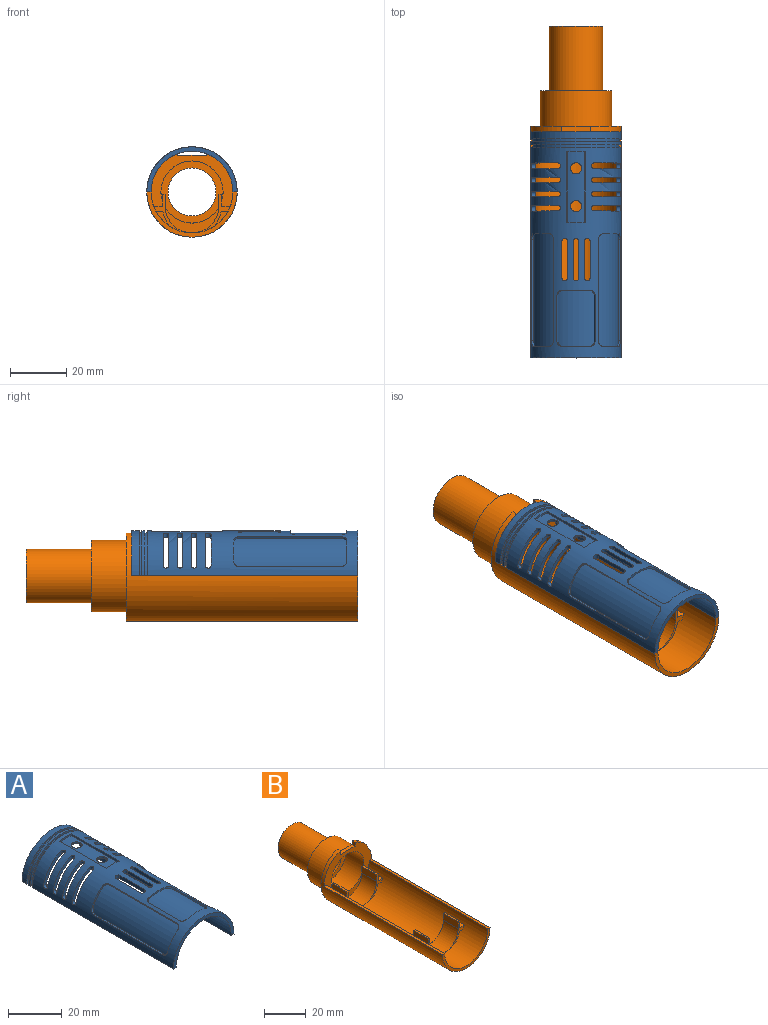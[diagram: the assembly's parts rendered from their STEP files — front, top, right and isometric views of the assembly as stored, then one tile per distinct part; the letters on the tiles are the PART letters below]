
ASSEMBLY  parts=2 mates=1
PART A: 92 faces, bbox 32x80x16 mm
  f0: cylinder r=16mm len=32mm, axis (0,1,0), area 50.3mm2, adj f5,f6,f87,f91
  f1: cylinder r=16mm len=32mm, axis (0,1,0), area 125.7mm2, adj f5,f6,f8,f88
  f2: cylinder r=14.5mm len=80mm, axis (0,1,0), area 3293.1mm2, adj f5,f6,f7,f8,f13,f14,f15,f16
  f3: cylinder r=15.25mm len=25mm, axis (0,1,0), area 134.5mm2, adj f9,f10,f11,f12,f45,f46
  f4: cylinder r=16mm len=74.5mm, axis (0,1,0), area 1885.3mm2, adj f5,f6,f7,f9,f10,f11,f12,f13
  f5: plane 80x1.5mm, normal (0,0,-1), area 118.5mm2, adj f0,f1,f2,f4,f7,f8,f86,f87
  f6: plane 80x1.5mm, normal (0,0,-1), area 118.5mm2, adj f0,f1,f2,f4,f7,f8,f86,f87
  f7: plane 32x16mm, normal (0,-1,0), area 71.9mm2, adj f2,f4,f5,f6
  f8: plane 32x16mm, normal (0,1,0), area 71.9mm2, adj f1,f2,f5,f6
  f9: plane 25x0.73mm, normal (0.98,0,0.21), area 18.8mm2, adj f3,f4,f11,f12
  f10: plane 25x0.73mm, normal (-0.98,0,0.21), area 18.8mm2, adj f3,f4,f11,f12
  f11: plane 6.65x1.08mm, normal (0,1,0), area 4.9mm2, adj f3,f4,f9,f10
  f12: plane 6.65x1.08mm, normal (0,-1,0), area 4.9mm2, adj f3,f4,f9,f10
  f13: plane 11.17x9.67mm, normal (0,-1,0), area 21mm2, adj f2,f4,f17,f18
  f14: plane 11.17x9.67mm, normal (0,1,0), area 21mm2, adj f2,f4,f17,f18
  f15: plane 11.17x9.67mm, normal (0,-1,0), area 21mm2, adj f2,f4,f19,f20
  f16: plane 11.17x9.67mm, normal (0,1,0), area 21mm2, adj f2,f4,f19,f20
  f17: cylinder r=1mm len=2mm, axis (-0.98,0,-0.17), area 4.7mm2, adj f2,f4,f13,f14
  f18: cylinder r=1mm len=2mm, axis (0.34,0,0.94), area 4.7mm2, adj f2,f4,f13,f14
  f19: cylinder r=1mm len=2mm, axis (-0.98,0,0.17), area 4.7mm2, adj f2,f4,f15,f16
  f20: cylinder r=1mm len=2mm, axis (0.34,0,-0.94), area 4.7mm2, adj f2,f4,f15,f16
  f21: plane 11.17x9.67mm, normal (0,-1,0), area 21mm2, adj f2,f4,f25,f26
  f22: plane 11.17x9.67mm, normal (0,1,0), area 21mm2, adj f2,f4,f25,f26
  f23: plane 11.17x9.67mm, normal (0,-1,0), area 21mm2, adj f2,f4,f27,f28
  f24: plane 11.17x9.67mm, normal (0,1,0), area 21mm2, adj f2,f4,f27,f28
  f25: cylinder r=1mm len=2mm, axis (-0.98,0,-0.17), area 4.7mm2, adj f2,f4,f21,f22
  f26: cylinder r=1mm len=2mm, axis (0.34,0,0.94), area 4.7mm2, adj f2,f4,f21,f22
  f27: cylinder r=1mm len=2mm, axis (-0.98,0,0.17), area 4.7mm2, adj f2,f4,f23,f24
  f28: cylinder r=1mm len=2mm, axis (0.34,0,-0.94), area 4.7mm2, adj f2,f4,f23,f24
  f29: plane 11.17x9.67mm, normal (0,-1,0), area 21mm2, adj f2,f4,f33,f34
  f30: plane 11.17x9.67mm, normal (0,1,0), area 21mm2, adj f2,f4,f33,f34
  f31: plane 11.17x9.67mm, normal (0,-1,0), area 21mm2, adj f2,f4,f35,f36
  f32: plane 11.17x9.67mm, normal (0,1,0), area 21mm2, adj f2,f4,f35,f36
  f33: cylinder r=1mm len=2mm, axis (-0.98,0,-0.17), area 4.7mm2, adj f2,f4,f29,f30
  f34: cylinder r=1mm len=2mm, axis (0.34,0,0.94), area 4.7mm2, adj f2,f4,f29,f30
  f35: cylinder r=1mm len=2mm, axis (-0.98,0,0.17), area 4.7mm2, adj f2,f4,f31,f32
  f36: cylinder r=1mm len=2mm, axis (0.34,0,-0.94), area 4.7mm2, adj f2,f4,f31,f32
  f37: plane 11.17x9.67mm, normal (0,-1,0), area 21mm2, adj f2,f4,f41,f42
  f38: plane 11.17x9.67mm, normal (0,1,0), area 21mm2, adj f2,f4,f41,f42
  f39: plane 11.17x9.67mm, normal (0,-1,0), area 21mm2, adj f2,f4,f43,f44
  f40: plane 11.17x9.67mm, normal (0,1,0), area 21mm2, adj f2,f4,f43,f44
  f41: cylinder r=1mm len=2mm, axis (-0.98,0,0.17), area 4.7mm2, adj f2,f4,f37,f38
  f42: cylinder r=1mm len=2mm, axis (0.34,0,-0.94), area 4.7mm2, adj f2,f4,f37,f38
  f43: cylinder r=1mm len=2mm, axis (-0.98,0,-0.17), area 4.7mm2, adj f2,f4,f39,f40
  f44: cylinder r=1mm len=2mm, axis (0.34,0,0.94), area 4.7mm2, adj f2,f4,f39,f40
  f45: cylinder r=2mm len=4mm, axis (0,0,-1), area 9.5mm2, adj f2,f3
  f46: cylinder r=2mm len=4mm, axis (0,0,-1), area 9.5mm2, adj f2,f3
  f47: plane 13x1.5mm, normal (-1,0,0), area 19.5mm2, adj f2,f4,f84,f85
  f48: plane 13x1.5mm, normal (1,0,0), area 19.5mm2, adj f2,f4,f84,f85
  f49: plane 13x1.53mm, normal (1,0,0), area 19.9mm2, adj f2,f4,f82,f83
  f50: plane 13x1.59mm, normal (-1,0,0), area 20.6mm2, adj f2,f4,f82,f83
  f51: plane 13x1.53mm, normal (-1,0,0), area 19.9mm2, adj f2,f4,f80,f81
  f52: plane 13x1.59mm, normal (1,0,0), area 20.6mm2, adj f2,f4,f80,f81
  f53: plane 36x0.65mm, normal (0.87,0,-0.5), area 27mm2, adj f4,f54,f72,f74
  f54: cylinder r=15.25mm len=40mm, axis (0,1,0), area 507.6mm2, adj f53,f55,f56,f57,f72,f73,f74,f75
  f55: plane 36x0.73mm, normal (-0.21,0,0.98), area 27mm2, adj f4,f54,f73,f75
  f56: plane 7.65x5.82mm, normal (0,1,0), area 6.8mm2, adj f4,f54,f74,f75
  f57: plane 7.65x5.82mm, normal (0,-1,0), area 6.8mm2, adj f4,f54,f72,f73
  f58: plane 36x0.65mm, normal (-0.87,0,-0.5), area 27mm2, adj f4,f60,f77,f79
  f59: plane 36x0.73mm, normal (0.21,0,0.98), area 27mm2, adj f4,f60,f76,f78
  f60: cylinder r=15.25mm len=40mm, axis (0,1,0), area 507.6mm2, adj f58,f59,f61,f62,f76,f77,f78,f79
  f61: plane 7.65x5.82mm, normal (0,1,0), area 6.8mm2, adj f4,f60,f78,f79
  f62: plane 7.65x5.82mm, normal (0,-1,0), area 6.8mm2, adj f4,f60,f76,f77
  f63: plane 16x0.68mm, normal (-0.91,0,0.42), area 12mm2, adj f4,f65,f69,f71
  f64: plane 16x0.68mm, normal (0.91,0,0.42), area 12mm2, adj f4,f65,f68,f70
  f65: cylinder r=15.25mm len=20mm, axis (0,1,0), area 262.7mm2, adj f63,f64,f66,f67,f68,f69,f70,f71
  f66: plane 9.79x1.45mm, normal (0,1,0), area 7.2mm2, adj f4,f65,f70,f71
  f67: plane 9.79x1.45mm, normal (0,-1,0), area 7.2mm2, adj f4,f65,f68,f69
  f68: cylinder r=2mm len=2.19mm, axis (-0.42,0,0.91), area 2.4mm2, adj f4,f64,f65,f67
  f69: cylinder r=2mm len=2.19mm, axis (-0.42,0,-0.91), area 2.4mm2, adj f4,f63,f65,f67
  f70: cylinder r=2mm len=2.19mm, axis (0.42,0,-0.91), area 2.4mm2, adj f4,f64,f65,f66
  f71: cylinder r=2mm len=2.19mm, axis (0.42,0,0.91), area 2.4mm2, adj f4,f63,f65,f66
  f72: cylinder r=2mm len=2.17mm, axis (0.5,0,0.87), area 2.4mm2, adj f4,f53,f54,f57
  f73: cylinder r=2mm len=2.14mm, axis (-0.98,0,-0.21), area 2.4mm2, adj f4,f54,f55,f57
  f74: cylinder r=2mm len=2.17mm, axis (-0.5,0,-0.87), area 2.4mm2, adj f4,f53,f54,f56
  f75: cylinder r=2mm len=2.14mm, axis (0.98,0,0.21), area 2.4mm2, adj f4,f54,f55,f56
  f76: cylinder r=2mm len=2.14mm, axis (-0.98,0,0.21), area 2.4mm2, adj f4,f59,f60,f62
  f77: cylinder r=2mm len=2.17mm, axis (0.5,0,-0.87), area 2.4mm2, adj f4,f58,f60,f62
  f78: cylinder r=2mm len=2.14mm, axis (0.98,0,-0.21), area 2.4mm2, adj f4,f59,f60,f61
  f79: cylinder r=2mm len=2.17mm, axis (-0.5,0,0.87), area 2.4mm2, adj f4,f58,f60,f61
  f80: cylinder r=1mm len=2.11mm, axis (0,0,1), area 4.9mm2, adj f2,f4,f51,f52
  f81: cylinder r=1mm len=2.11mm, axis (0,0,1), area 4.9mm2, adj f2,f4,f51,f52
  f82: cylinder r=1mm len=2.11mm, axis (0,0,1), area 4.9mm2, adj f2,f4,f49,f50
  f83: cylinder r=1mm len=2.11mm, axis (0,0,-1), area 4.9mm2, adj f2,f4,f49,f50
  f84: cylinder r=1mm len=2mm, axis (0,0,1), area 4.7mm2, adj f2,f4,f47,f48
  f85: cylinder r=1mm len=2mm, axis (0,0,1), area 4.7mm2, adj f2,f4,f47,f48
  f86: cylinder r=15.25mm len=30.5mm, axis (0,1,0), area 47.9mm2, adj f5,f6,f87,f88
  f87: plane 32x16mm, normal (0,1,0), area 36.8mm2, adj f0,f5,f6,f86
  f88: plane 32x16mm, normal (0,-1,0), area 36.8mm2, adj f1,f5,f6,f86
  f89: cylinder r=15.25mm len=30.5mm, axis (0,1,0), area 47.9mm2, adj f5,f6,f90,f91
  f90: plane 32x16mm, normal (0,1,0), area 36.8mm2, adj f4,f5,f6,f89
  f91: plane 32x16mm, normal (0,-1,0), area 36.8mm2, adj f0,f5,f6,f89
PART B: 52 faces, bbox 32x117.5x31.2 mm
  f0: cylinder r=14.5mm len=80mm, axis (0,1,0), area 3248.4mm2, adj f2,f3,f4,f17,f18,f19,f20,f22
  f1: plane 18.97x8.93mm, normal (0,-1,0), area 58mm2, adj f11,f21
  f2: plane 32x20.2mm, normal (0,-1,0), area 219.6mm2, adj f0,f5,f6,f7,f8,f11,f17,f18
  f3: plane 5.5x5.35mm, normal (0,-1,0), area 7.2mm2, adj f0,f20,f26
  f4: plane 5.5x5.35mm, normal (0,-1,0), area 7.2mm2, adj f0,f27,f28
  f5: cylinder r=16mm len=82mm, axis (0,-1,0), area 4202mm2, adj f2,f6,f8,f9,f17,f18,f19
  f6: plane 2.2x2mm, normal (-1,0,0), area 4.4mm2, adj f2,f5,f7,f9
  f7: plane 10x2mm, normal (0,0,1), area 20mm2, adj f2,f6,f8,f9
  f8: plane 2.2x2mm, normal (1,0,0), area 4.4mm2, adj f2,f5,f7,f9
  f9: plane 32x31.2mm, normal (0,1,0), area 274.2mm2, adj f5,f6,f7,f8,f10
  f10: cylinder r=12.65mm len=25.3mm, axis (0,-1,0), area 993.5mm2, adj f9,f13
  f11: cylinder r=11mm len=22mm, axis (0,-1,0), area 863.9mm2, adj f1,f2,f12,f24,f25
  f12: plane 22x22mm, normal (0,-1,0), area 153.2mm2, adj f11,f14
  f13: plane 25.3x25.3mm, normal (0,1,0), area 219.2mm2, adj f10,f15
  f14: cylinder r=8.5mm len=25mm, axis (0,-1,0), area 1335.2mm2, adj f12,f16
  f15: cylinder r=9.5mm len=23mm, axis (0,-1,0), area 1372.9mm2, adj f13,f16
  f16: plane 19x19mm, normal (0,1,0), area 56.5mm2, adj f14,f15
  f17: plane 80x1.5mm, normal (0,0,1), area 120mm2, adj f0,f2,f5,f19
  f18: plane 80x1.5mm, normal (0,0,1), area 120mm2, adj f0,f2,f5,f19
  f19: plane 32x16mm, normal (0,-1,0), area 71.9mm2, adj f0,f5,f17,f18
  f20: cylinder r=10.5mm len=10mm, axis (0,1,0), area 63.4mm2, adj f0,f3,f23,f26
  f21: cylinder r=9.5mm len=19mm, axis (0,1,0), area 298.5mm2, adj f1,f22,f23,f24,f25,f32,f33
  f22: plane 13.61x13.5mm, normal (0,-1,0), area 20mm2, adj f0,f21,f27,f28,f29,f30,f31,f32
  f23: plane 13.61x13.5mm, normal (0,-1,0), area 20mm2, adj f0,f20,f21,f26,f33,f34,f35,f36
  f24: plane 4.58x1.02mm, normal (0,1,0), area 3.5mm2, adj f11,f21,f30,f31,f32
  f25: plane 4.58x1.02mm, normal (0,1,0), area 3.5mm2, adj f11,f21,f33,f34,f35
  f26: plane 10x2.39mm, normal (0,0,-1), area 23.9mm2, adj f0,f3,f20,f23
  f27: cylinder r=10.5mm len=10mm, axis (0,1,0), area 63.4mm2, adj f0,f4,f22,f28
  f28: plane 10x2.39mm, normal (0,0,-1), area 23.9mm2, adj f0,f4,f22,f27
  f29: plane 10x3.11mm, normal (0,0,1), area 31.1mm2, adj f0,f2,f22,f30
  f30: plane 10x4mm, normal (1,0,0), area 40mm2, adj f2,f22,f24,f29,f31
  f31: plane 10x1mm, normal (0,0,1), area 10mm2, adj f22,f24,f30,f32
  f32: plane 10x4mm, normal (-1,0,0), area 40mm2, adj f21,f22,f24,f31
  f33: plane 10x4mm, normal (1,0,0), area 40mm2, adj f21,f23,f25,f34
  f34: plane 10x1mm, normal (0,0,1), area 10mm2, adj f23,f25,f33,f35
  f35: plane 10x4mm, normal (-1,0,0), area 40mm2, adj f2,f23,f25,f34,f36
  f36: plane 10x3.11mm, normal (0,0,1), area 31.1mm2, adj f0,f2,f23,f35
  f37: cylinder r=10.5mm len=10mm, axis (0,-1,0), area 63.7mm2, adj f0,f38,f39,f49
  f38: plane 27.23x13.51mm, normal (0,1,0), area 40.1mm2, adj f0,f37,f40,f41,f42,f43,f44,f45
  f39: plane 27.23x13.51mm, normal (0,-1,0), area 40.1mm2, adj f0,f37,f40,f41,f42,f43,f44,f45
  f40: plane 10x3.11mm, normal (0,0,1), area 31.1mm2, adj f0,f38,f39,f41
  f41: plane 10x4mm, normal (1,0,0), area 40mm2, adj f38,f39,f40,f42
  f42: plane 10x1mm, normal (0,0,1), area 10mm2, adj f38,f39,f41,f43
  f43: plane 10x4mm, normal (-1,0,0), area 40mm2, adj f38,f39,f42,f44
  f44: cylinder r=9.5mm len=19mm, axis (0,-1,0), area 298.5mm2, adj f38,f39,f43,f45
  f45: plane 10x4mm, normal (1,0,0), area 40mm2, adj f38,f39,f44,f46
  f46: plane 10x1mm, normal (0,0,1), area 10mm2, adj f38,f39,f45,f47
  f47: plane 10x4mm, normal (-1,0,0), area 40mm2, adj f38,f39,f46,f48
  f48: plane 10x3.11mm, normal (0,0,1), area 31.1mm2, adj f0,f38,f39,f47
  f49: plane 10x2.39mm, normal (0,0,-1), area 23.9mm2, adj f0,f37,f38,f39
  f50: cylinder r=10.5mm len=10mm, axis (0,-1,0), area 63.7mm2, adj f0,f38,f39,f51
  f51: plane 10x2.39mm, normal (0,0,-1), area 23.9mm2, adj f0,f38,f39,f50
PLACE A t=(-86.74,63.69,16.22)mm
PLACE B t=(-31.74,63.69,16.22)mm
MATE fastened B.f17 <-> A.f6  axis (0,0,1) through (-46.99,-16.31,16.22)mm
